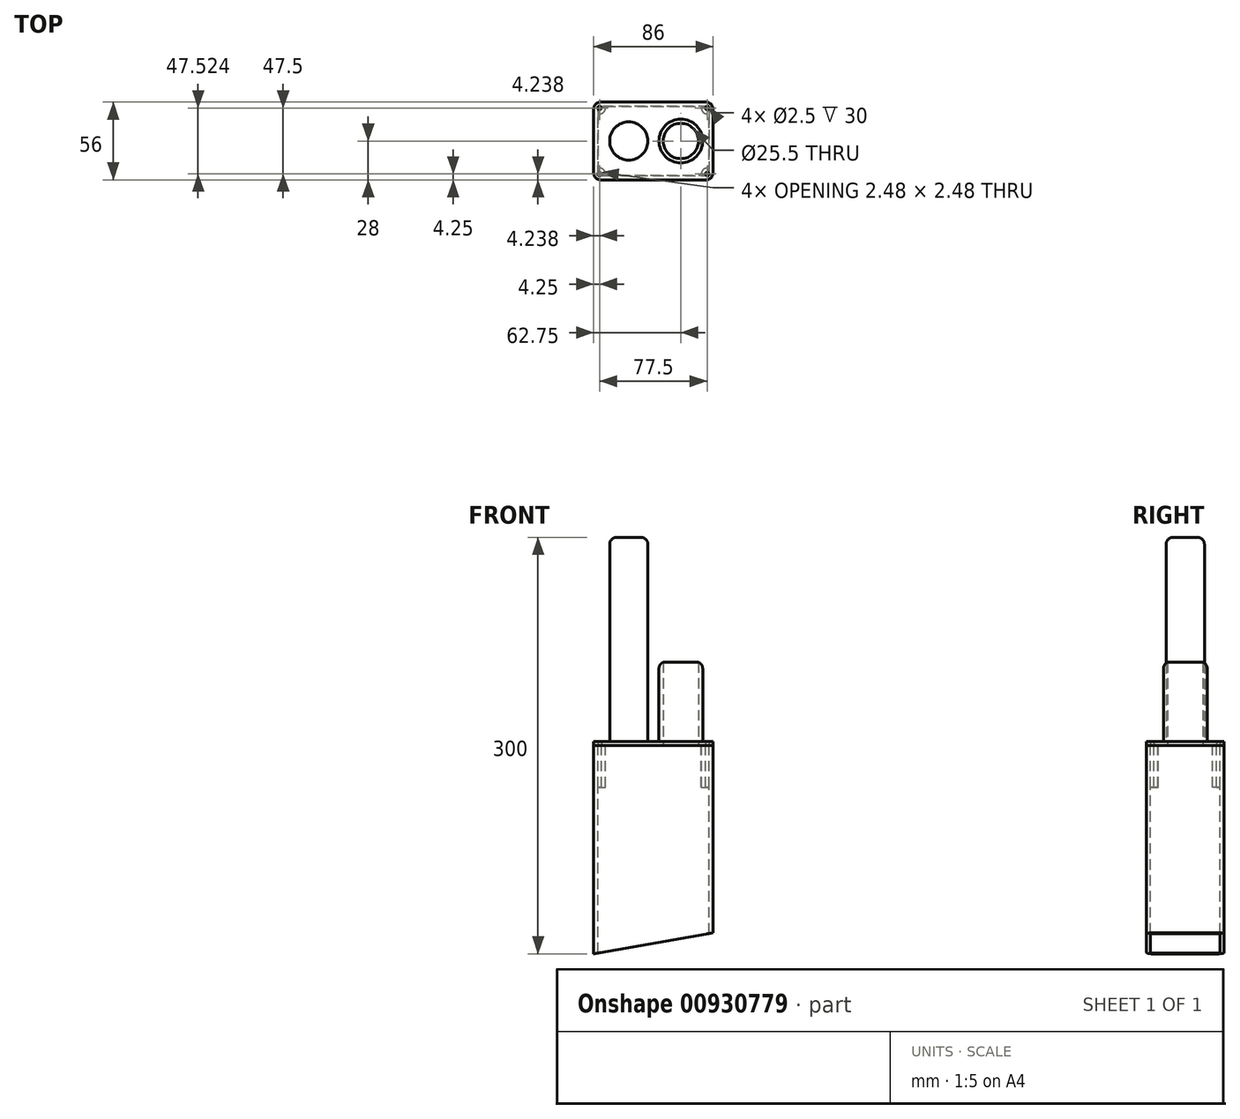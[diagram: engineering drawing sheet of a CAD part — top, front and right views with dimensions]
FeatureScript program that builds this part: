
annotation { "Feature Type Name" : "Feature", "Feature Type Description" : "" }
export const myFeature = defineFeature(function(context is Context, id is Id, definition is map)
    precondition{}
    {
        {
            var Q0;
            Q0=qCreatedBy(makeId("Top.planeOp"),FACE);
            var sketch = newSketch(context, id + "F0", { "sketchPlane" : qUnion([Q0])});
            skCircle(sketch, "E0", {"center": v(19.75, 0) * mm, "radius": 15.75 * mm});
            skCircle(sketch, "E1", {"center": v(-17.75, 0) * mm, "radius": 13.75 * mm});
            skCircle(sketch, "E2", {"center": v(19.75, 0) * mm, "radius": 12.75 * mm});
            skLineSegment(sketch, "E3.bottom", {"start": v(-43, 28) * mm, "end": v(43, 28) * mm});
            skLineSegment(sketch, "E3.top", {"start": v(-43, -28) * mm, "end": v(43, -28) * mm});
            skLineSegment(sketch, "E3.left", {"start": v(-43, 28) * mm, "end": v(-43, -28) * mm});
            skLineSegment(sketch, "E3.right", {"start": v(43, 28) * mm, "end": v(43, -28) * mm});
            skLineSegment(sketch, "E4.bottom", {"start": v(-40, 25) * mm, "end": v(40, 25) * mm});
            skLineSegment(sketch, "E4.top", {"start": v(-40, -25) * mm, "end": v(40, -25) * mm});
            skLineSegment(sketch, "E4.left", {"start": v(-40, 25) * mm, "end": v(-40, -25) * mm});
            skLineSegment(sketch, "E4.right", {"start": v(40, 25) * mm, "end": v(40, -25) * mm});
            skCircle(sketch, "E5", {"center": v(-38.75, -23.75) * mm, "radius": 1.25 * mm});
            skArc(sketch, "E6", {"start": v(-34.69, -25) * mm, "mid": v(-35.74, -20.74) * mm, "end": v(-40, -19.69) * mm});
            skCircle(sketch, "E7", {"center": v(38.75, -23.75) * mm, "radius": 1.25 * mm});
            skArc(sketch, "E8", {"start": v(40, -19.69) * mm, "mid": v(35.74, -20.74) * mm, "end": v(34.69, -25) * mm});
            skCircle(sketch, "E9", {"center": v(-38.75, 23.75) * mm, "radius": 1.25 * mm});
            skArc(sketch, "E10", {"start": v(-40, 19.69) * mm, "mid": v(-35.74, 20.74) * mm, "end": v(-34.69, 25) * mm});
            skCircle(sketch, "E11", {"center": v(38.75, 23.75) * mm, "radius": 1.25 * mm});
            skArc(sketch, "E12", {"start": v(34.69, 25) * mm, "mid": v(35.74, 20.74) * mm, "end": v(40, 19.69) * mm});
            skSolve(sketch);
        }
        {
            var Q0;
            Q0=makeQuery(id+"F0.imprint","IMPRINT",FACE,{"disambiguationData":[TD([[makeQuery(id+"F0.imprint","IMPRINT",EDGE,{"derivedFrom":sQuery(id+"F0.wireOp",EDGE,"E3.bottom")}),-1.0]])]});
            extrude(context, id + "F1", {"entities" : qUnion([Q0]), "oppositeDirection" : true, "depth" : 150 * mm, "offsetDistance" : 25 * mm});
        }
        {
            var Q0;
            {var subQ0=sQuery(id+"F0.wireOp",EDGE,"E10");Q0=makeQuery(id+"F0.imprint","IMPRINT",FACE,{"disambiguationData":[TD([[makeQuery(id+"F0.imprint","IMPRINT",EDGE,{"derivedFrom":subQ0}),1.0]])]});}
            var Q1;
            {var subQ0=sQuery(id+"F0.wireOp",EDGE,"E12");Q1=makeQuery(id+"F0.imprint","IMPRINT",FACE,{"disambiguationData":[TD([[makeQuery(id+"F0.imprint","IMPRINT",EDGE,{"derivedFrom":subQ0}),1.0]])]});}
            var Q2;
            {var subQ0=sQuery(id+"F0.wireOp",EDGE,"E6");Q2=makeQuery(id+"F0.imprint","IMPRINT",FACE,{"disambiguationData":[TD([[makeQuery(id+"F0.imprint","IMPRINT",EDGE,{"derivedFrom":subQ0}),1.0]])]});}
            var Q3;
            {var subQ0=sQuery(id+"F0.wireOp",EDGE,"E8");Q3=makeQuery(id+"F0.imprint","IMPRINT",FACE,{"disambiguationData":[TD([[makeQuery(id+"F0.imprint","IMPRINT",EDGE,{"derivedFrom":subQ0}),1.0]])]});}
            var Q4;
            {var subQ0=sQuery(id+"F0.wireOp",EDGE,"E4.left");var subQ1=sQuery(id+"F0.wireOp",EDGE,"E4.bottom");var subQ2=makeQuery(id+"F0.imprint","INTERSECT",VERTEX,{"derivedFrom":[subQ1,subQ0]});Q4=makeQuery(id+"F0.imprint","IMPRINT",FACE,{"disambiguationData":[TD([[makeQuery(id+"F0.imprint","IMPRINT",EDGE,{"disambiguationData":[TD([[subQ2,-1.0]])],"derivedFrom":subQ1}),-1.0]])]});}
            var Q5;
            {var subQ0=sQuery(id+"F0.wireOp",EDGE,"E4.right");var subQ1=sQuery(id+"F0.wireOp",EDGE,"E4.bottom");var subQ2=makeQuery(id+"F0.imprint","INTERSECT",VERTEX,{"derivedFrom":[subQ1,subQ0]});Q5=makeQuery(id+"F0.imprint","IMPRINT",FACE,{"disambiguationData":[TD([[makeQuery(id+"F0.imprint","IMPRINT",EDGE,{"disambiguationData":[TD([[subQ2,1.0]])],"derivedFrom":subQ1}),-1.0]])]});}
            var Q6;
            {var subQ0=sQuery(id+"F0.wireOp",EDGE,"E4.right");var subQ1=sQuery(id+"F0.wireOp",EDGE,"E4.top");var subQ2=makeQuery(id+"F0.imprint","INTERSECT",VERTEX,{"derivedFrom":[subQ1,subQ0]});Q6=makeQuery(id+"F0.imprint","IMPRINT",FACE,{"disambiguationData":[TD([[makeQuery(id+"F0.imprint","IMPRINT",EDGE,{"disambiguationData":[TD([[subQ2,1.0]])],"derivedFrom":subQ1}),1.0]])]});}
            var Q7;
            {var subQ0=sQuery(id+"F0.wireOp",EDGE,"E4.left");var subQ1=sQuery(id+"F0.wireOp",EDGE,"E4.top");var subQ2=makeQuery(id+"F0.imprint","INTERSECT",VERTEX,{"derivedFrom":[subQ1,subQ0]});Q7=makeQuery(id+"F0.imprint","IMPRINT",FACE,{"disambiguationData":[TD([[makeQuery(id+"F0.imprint","IMPRINT",EDGE,{"disambiguationData":[TD([[subQ2,-1.0]])],"derivedFrom":subQ1}),1.0]])]});}
            extrude(context, id + "F2", {"entities" : qUnion([Q0, Q1, Q2, Q3, Q4, Q5, Q6, Q7]), "operationType" : NewBodyOperationType.ADD, "oppositeDirection" : true, "depth" : 30 * mm, "offsetDistance" : 25 * mm});
        }
        {
            var Q0;
            Q0 = qSketchRegion(id + "F0", true);
            var Q1;
            Q1=makeQuery(id+"F0.imprint","IMPRINT",FACE,{"disambiguationData":[TD([[makeQuery(id+"F0.imprint","IMPRINT",EDGE,{"derivedFrom":sQuery(id+"F0.wireOp",EDGE,"E0")}),-1.0]])]});
            var Q2;
            {var subQ0=sQuery(id+"F0.wireOp",EDGE,"E10");Q2=makeQuery(id+"F0.imprint","IMPRINT",FACE,{"disambiguationData":[TD([[makeQuery(id+"F0.imprint","IMPRINT",EDGE,{"derivedFrom":subQ0}),1.0]])]});}
            var Q3;
            {var subQ0=sQuery(id+"F0.wireOp",EDGE,"E6");Q3=makeQuery(id+"F0.imprint","IMPRINT",FACE,{"disambiguationData":[TD([[makeQuery(id+"F0.imprint","IMPRINT",EDGE,{"derivedFrom":subQ0}),1.0]])]});}
            var Q4;
            {var subQ0=sQuery(id+"F0.wireOp",EDGE,"E8");Q4=makeQuery(id+"F0.imprint","IMPRINT",FACE,{"disambiguationData":[TD([[makeQuery(id+"F0.imprint","IMPRINT",EDGE,{"derivedFrom":subQ0}),1.0]])]});}
            var Q5;
            {var subQ0=sQuery(id+"F0.wireOp",EDGE,"E12");Q5=makeQuery(id+"F0.imprint","IMPRINT",FACE,{"disambiguationData":[TD([[makeQuery(id+"F0.imprint","IMPRINT",EDGE,{"derivedFrom":subQ0}),1.0]])]});}
            extrude(context, id + "F3", {"entities" : qUnion([Q0, Q1, Q2, Q3, Q4, Q5]), "depth" : 3 * mm, "offsetDistance" : 25 * mm});
        }
        {
            var Q0;
            Q0=makeQuery(id+"F0.imprint","IMPRINT",FACE,{"disambiguationData":[TD([[makeQuery(id+"F0.imprint","IMPRINT",EDGE,{"derivedFrom":sQuery(id+"F0.wireOp",EDGE,"E0")}),1.0]])]});
            extrude(context, id + "F4", {"entities" : qUnion([Q0]), "operationType" : NewBodyOperationType.ADD, "depth" : 60 * mm, "offsetDistance" : 25 * mm});
        }
        {
            var Q0;
            Q0=makeQuery(id+"F0.imprint","IMPRINT",FACE,{"disambiguationData":[TD([[makeQuery(id+"F0.imprint","IMPRINT",EDGE,{"derivedFrom":sQuery(id+"F0.wireOp",EDGE,"E1")}),1.0]])]});
            extrude(context, id + "F5", {"entities" : qUnion([Q0]), "operationType" : NewBodyOperationType.ADD, "depth" : 150 * mm, "offsetDistance" : 25 * mm});
        }
        {
            var Q0;
            {var subQ0=sQuery(id+"F0.wireOp",EDGE,"E3.top");Q0=makeQuery(id+"F3.boolean.opBoolean","MERGE",FACE,{"derivedFrom":[makeQuery(id+"F1.opExtrude","SWEPT_FACE",FACE,{"disambiguationData":[OSD([subQ0])]}),makeQuery(id+"F3.opExtrude","SWEPT_FACE",FACE,{"disambiguationData":[OSD([subQ0])]})]});}
            var sketch = newSketch(context, id + "F6", { "sketchPlane" : qUnion([Q0])});
            skLineSegment(sketch, "E13", {"start": v(-43, -150) * mm, "end": v(43, -150) * mm});
            skLineSegment(sketch, "E14", {"start": v(43, -150) * mm, "end": v(43, -134.84) * mm});
            skLineSegment(sketch, "E15", {"start": v(43, -134.84) * mm, "end": v(-43, -150) * mm});
            skSolve(sketch);
        }
        {
            var Q0;
            Q0 = qSketchRegion(id + "F6", true);
            extrude(context, id + "F7", {"entities" : qUnion([Q0]), "operationType" : NewBodyOperationType.REMOVE, "endBound" : BoundingType.THROUGH_ALL, "oppositeDirection" : true, "depth" : 25 * mm, "offsetDistance" : 25 * mm});
        }
        {
            var Q0;
            Q0=makeQuery(id+"F1.opExtrude","SWEPT_EDGE",EDGE,{"disambiguationData":[OSD([sQuery(id+"F0.wireOp",EDGE,"E3.top"),sQuery(id+"F0.wireOp",EDGE,"E3.left")])]});
            var Q1;
            Q1=makeQuery(id+"F1.opExtrude","SWEPT_EDGE",EDGE,{"disambiguationData":[OSD([sQuery(id+"F0.wireOp",EDGE,"E3.top"),sQuery(id+"F0.wireOp",EDGE,"E3.right")])]});
            var Q2;
            Q2=makeQuery(id+"F1.opExtrude","SWEPT_EDGE",EDGE,{"disambiguationData":[OSD([sQuery(id+"F0.wireOp",EDGE,"E3.bottom"),sQuery(id+"F0.wireOp",EDGE,"E3.left")])]});
            var Q3;
            Q3=makeQuery(id+"F1.opExtrude","SWEPT_EDGE",EDGE,{"disambiguationData":[OSD([sQuery(id+"F0.wireOp",EDGE,"E3.bottom"),sQuery(id+"F0.wireOp",EDGE,"E3.right")])]});
            fillet(context, id + "F8", {"entities" : qUnion([Q0, Q1, Q2, Q3]), "radius" : 5 * mm, "allowEdgeOverflow" : false});
        }
        {
            var Q0;
            Q0=makeQuery(id+"F3.opExtrude","SWEPT_EDGE",EDGE,{"disambiguationData":[OSD([sQuery(id+"F0.wireOp",EDGE,"E3.top"),sQuery(id+"F0.wireOp",EDGE,"E3.right")])]});
            var Q1;
            Q1=makeQuery(id+"F3.opExtrude","SWEPT_EDGE",EDGE,{"disambiguationData":[OSD([sQuery(id+"F0.wireOp",EDGE,"E3.bottom"),sQuery(id+"F0.wireOp",EDGE,"E3.right")])]});
            var Q2;
            Q2=makeQuery(id+"F3.opExtrude","SWEPT_EDGE",EDGE,{"disambiguationData":[OSD([sQuery(id+"F0.wireOp",EDGE,"E3.bottom"),sQuery(id+"F0.wireOp",EDGE,"E3.left")])]});
            var Q3;
            Q3=makeQuery(id+"F3.opExtrude","SWEPT_EDGE",EDGE,{"disambiguationData":[OSD([sQuery(id+"F0.wireOp",EDGE,"E3.top"),sQuery(id+"F0.wireOp",EDGE,"E3.left")])]});
            var Q4;
            Q4=makeQuery(id+"F3.opExtrude","CAP_EDGE",EDGE,{"disambiguationData":[OSD([sQuery(id+"F0.wireOp",EDGE,"E0")])],"isStart":false});
            var Q5;
            Q5=makeQuery(id+"F3.opExtrude","CAP_EDGE",EDGE,{"disambiguationData":[OSD([sQuery(id+"F0.wireOp",EDGE,"E1")])],"isStart":false});
            var Q6;
            Q6=makeQuery(id+"F5.opExtrude","CAP_FACE",FACE,{"disambiguationData":[OSD([sQuery(id+"F0.wireOp",EDGE,"E1")])],"isStart":false});
            var Q7;
            Q7=makeQuery(id+"F4.opExtrude","CAP_EDGE",EDGE,{"disambiguationData":[OSD([sQuery(id+"F0.wireOp",EDGE,"E0")])],"isStart":false});
            fillet(context, id + "F9", {"entities" : qUnion([Q0, Q1, Q2, Q3, Q4, Q5, Q6, Q7]), "radius" : 5 * mm, "tangentPropagation" : true, "allowEdgeOverflow" : false});
        }
    });
